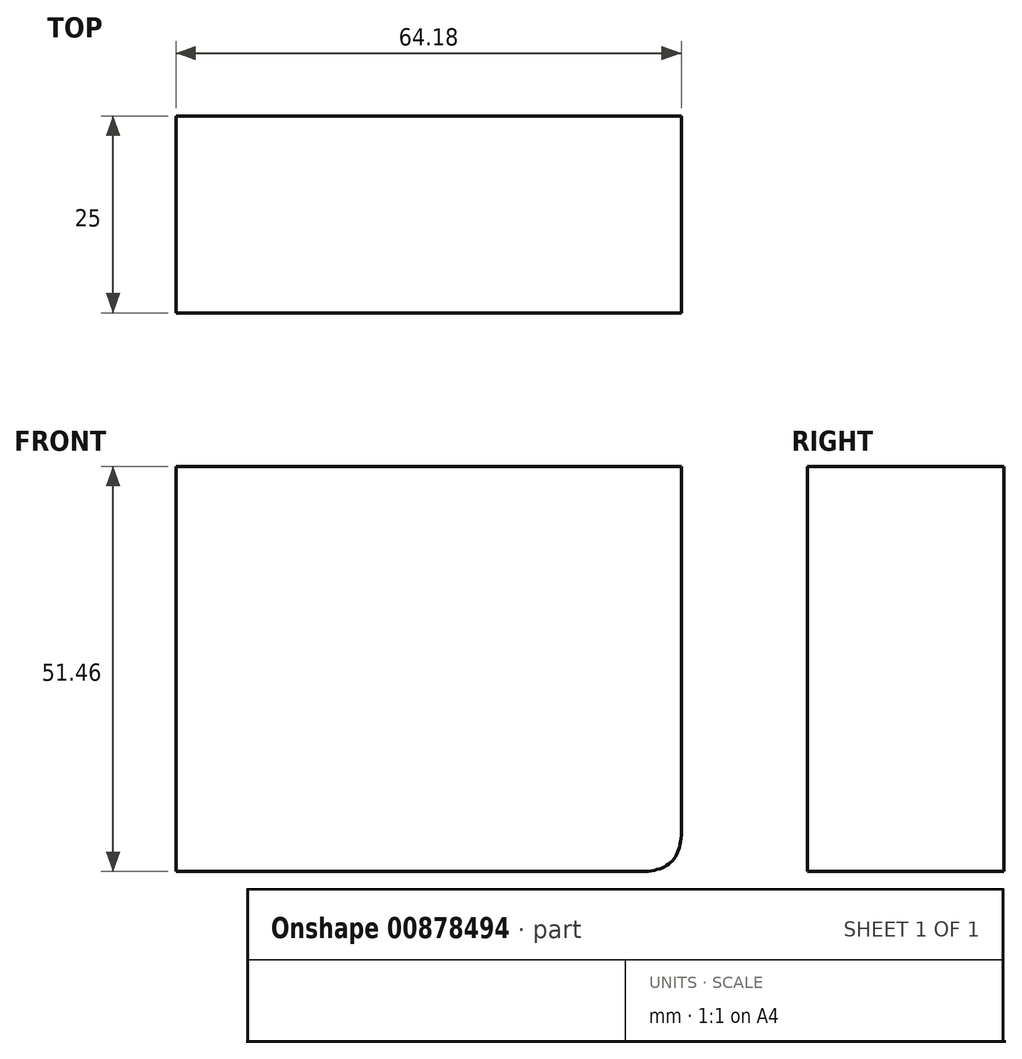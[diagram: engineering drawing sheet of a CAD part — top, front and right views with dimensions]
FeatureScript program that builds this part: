
annotation { "Feature Type Name" : "Feature", "Feature Type Description" : "" }
export const myFeature = defineFeature(function(context is Context, id is Id, definition is map)
    precondition{}
    {
        {
            var Q0;
            Q0=qCreatedBy(makeId("Front.planeOp"),FACE);
            var sketch = newSketch(context, id + "F0", { "sketchPlane" : qUnion([Q0])});
            skLineSegment(sketch, "E0.bottom", {"start": v(-176.48, 22.98) * mm, "end": v(-112.3, 22.98) * mm});
            skLineSegment(sketch, "E0.top", {"start": v(-176.48, 74.44) * mm, "end": v(-112.3, 74.44) * mm});
            skLineSegment(sketch, "E0.left", {"start": v(-176.48, 22.98) * mm, "end": v(-176.48, 74.44) * mm});
            skLineSegment(sketch, "E0.right", {"start": v(-112.3, 22.98) * mm, "end": v(-112.3, 74.44) * mm});
            skPoint(sketch, "E0.middle", {"position": v(-144.39, 48.7) * mm});
            skSolve(sketch);
        }
        {
            var Q0;
            Q0=makeQuery(id+"F0.imprint","IMPRINT",FACE,{"disambiguationData":[TD([[makeQuery(id+"F0.imprint","IMPRINT",EDGE,{"derivedFrom":sQuery(id+"F0.wireOp",EDGE,"E0.bottom")}),1.0]])]});
            extrude(context, id + "F1", {"entities" : qUnion([Q0]), "depth" : 25 * mm, "offsetDistance" : 25 * mm});
        }
        {
            var Q0;
            Q0=makeQuery(id+"F1.opExtrude","SWEPT_EDGE",EDGE,{"disambiguationData":[OSD([sQuery(id+"F0.wireOp",EDGE,"E0.bottom"),sQuery(id+"F0.wireOp",EDGE,"E0.right")])]});
            fillet(context, id + "F2", {"entities" : qUnion([Q0]), "radius" : 5 * mm, "tangentPropagation" : true, "rho" : 0.5, "crossSection" : FilletCrossSection.CONIC, "allowEdgeOverflow" : false});
        }
    });
